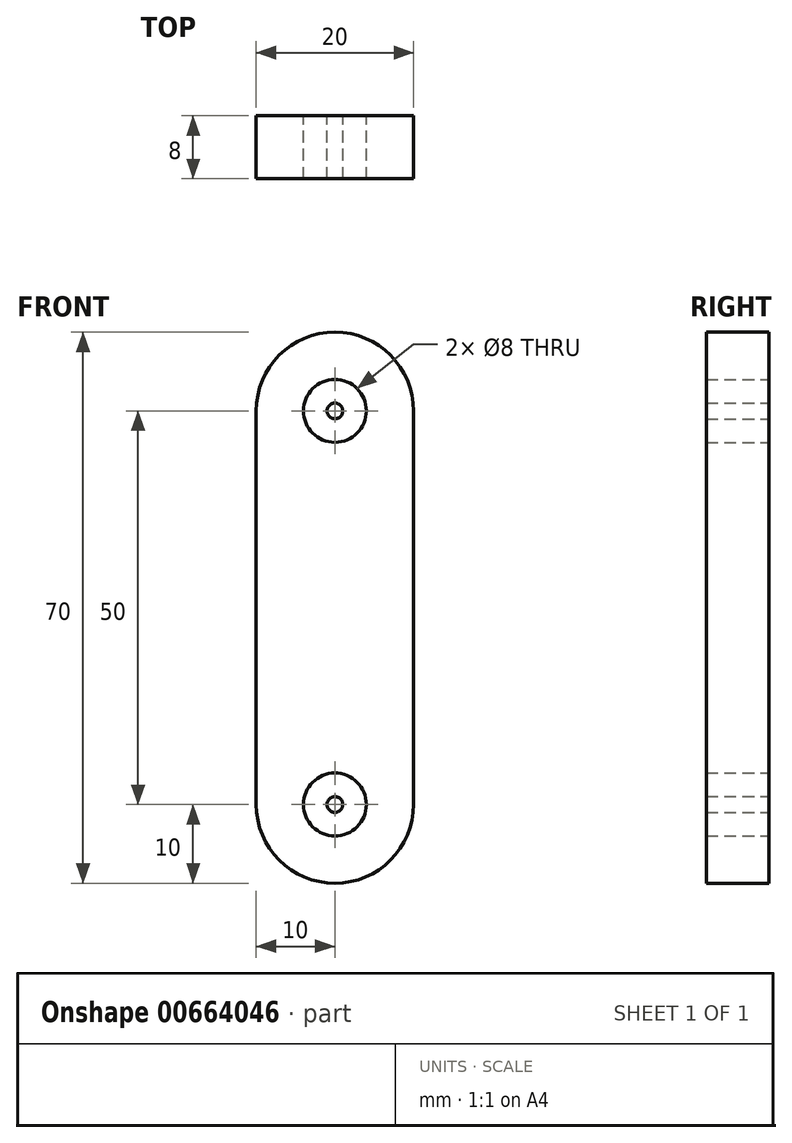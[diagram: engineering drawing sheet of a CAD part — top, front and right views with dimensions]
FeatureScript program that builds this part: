
annotation { "Feature Type Name" : "Feature", "Feature Type Description" : "" }
export const myFeature = defineFeature(function(context is Context, id is Id, definition is map)
    precondition{}
    {
        {
            var Q0;
            Q0=qCreatedBy(makeId("Front.planeOp"),FACE);
            var sketch = newSketch(context, id + "F0", { "sketchPlane" : qUnion([Q0])});
            skCircle(sketch, "E0", {"center": v(0, 0) * mm, "radius": 4 * mm});
            skArc(sketch, "E1", {"start": v(-10, 0) * mm, "mid": v(0, -10) * mm, "end": v(10, 0) * mm});
            skLineSegment(sketch, "E2", {"start": v(-10, 0) * mm, "end": v(-10, 50) * mm});
            skLineSegment(sketch, "E3", {"start": v(10, 0) * mm, "end": v(10, 50) * mm});
            skPoint(sketch, "E4.center.orphan", {"position": v(0, 50) * mm});
            skArc(sketch, "E5", {"start": v(10, 50) * mm, "mid": v(0, 60) * mm, "end": v(-10, 50) * mm});
            skCircle(sketch, "E6", {"center": v(0, 50) * mm, "radius": 4 * mm});
            skSolve(sketch);
        }
        {
            var Q0;
            Q0 = qSketchRegion(id + "F0", true);
            extrude(context, id + "F1", {"entities" : qUnion([Q0]), "depth" : 8 * mm, "offsetDistance" : 25.4 * mm});
        }
        {
            var Q0;
            Q0=qCreatedBy(makeId("Front.planeOp"),FACE);
            var sketch = newSketch(context, id + "F2", { "sketchPlane" : qUnion([Q0])});
            skCircle(sketch, "E7", {"center": v(0, 0) * mm, "radius": 1 * mm});
            skCircle(sketch, "E8", {"center": v(0, 50) * mm, "radius": 1 * mm});
            skSolve(sketch);
        }
        {
            var Q0;
            Q0 = qSketchRegion(id + "F2", true);
            extrude(context, id + "F3", {"entities" : qUnion([Q0]), "depth" : 8 * mm, "offsetDistance" : 25.4 * mm});
        }
    });
